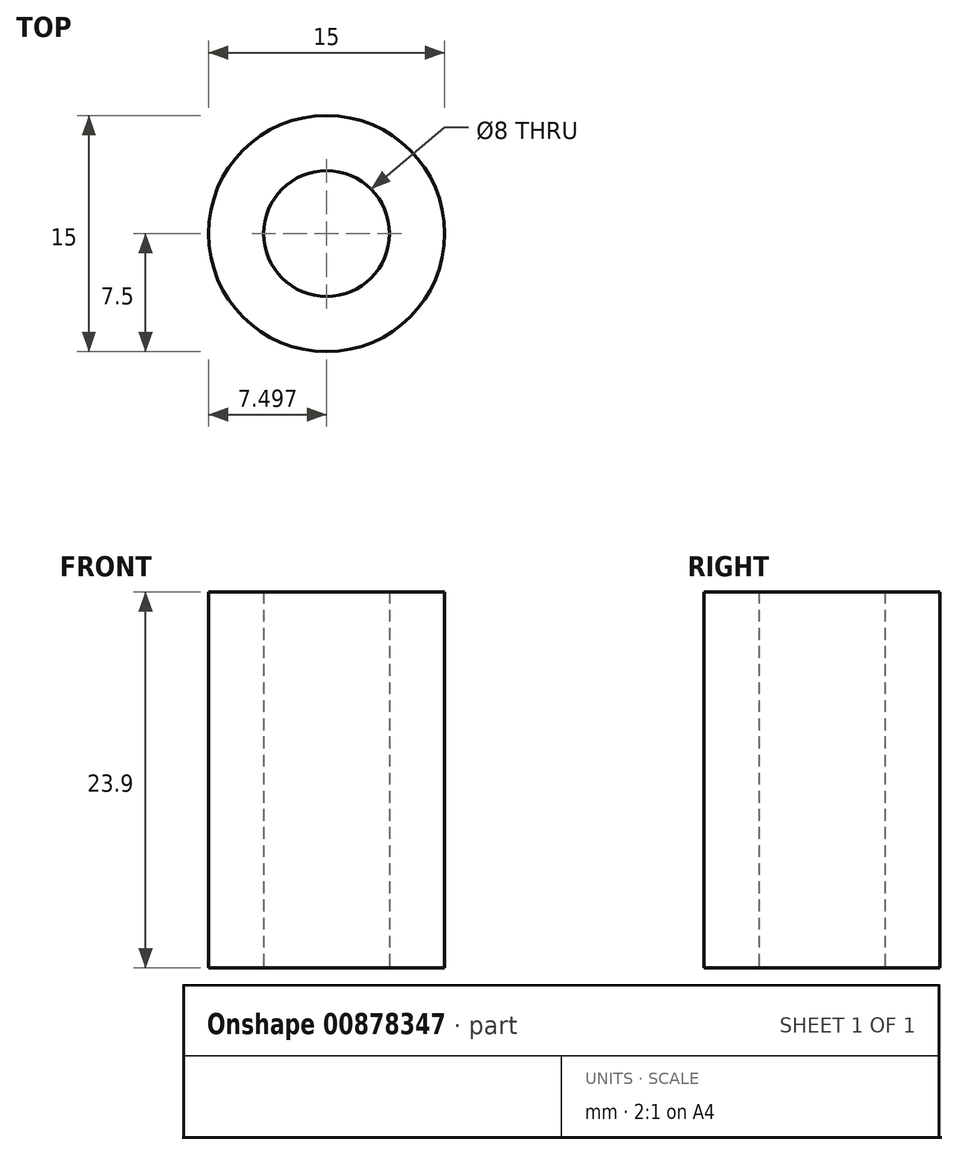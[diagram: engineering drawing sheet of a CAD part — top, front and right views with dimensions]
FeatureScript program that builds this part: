
annotation { "Feature Type Name" : "Feature", "Feature Type Description" : "" }
export const myFeature = defineFeature(function(context is Context, id is Id, definition is map)
    precondition{}
    {
        {
            var Q0;
            Q0=qCreatedBy(makeId("Top.planeOp"),FACE);
            var sketch = newSketch(context, id + "F0", { "sketchPlane" : qUnion([Q0])});
            skCircle(sketch, "E0", {"center": v(0.63, 0) * mm, "radius": 7.5 * mm});
            skCircle(sketch, "E1", {"center": v(0.63, 0) * mm, "radius": 4 * mm});
            skSolve(sketch);
        }
        {
            var Q0;
            Q0=makeQuery(id+"F0.imprint","IMPRINT",FACE,{"disambiguationData":[TD([[makeQuery(id+"F0.imprint","IMPRINT",EDGE,{"derivedFrom":sQuery(id+"F0.wireOp",EDGE,"E0")}),1.0]])]});
            extrude(context, id + "F1", {"entities" : qUnion([Q0]), "depth" : 23.9 * mm, "offsetDistance" : 25 * mm});
        }
    });
